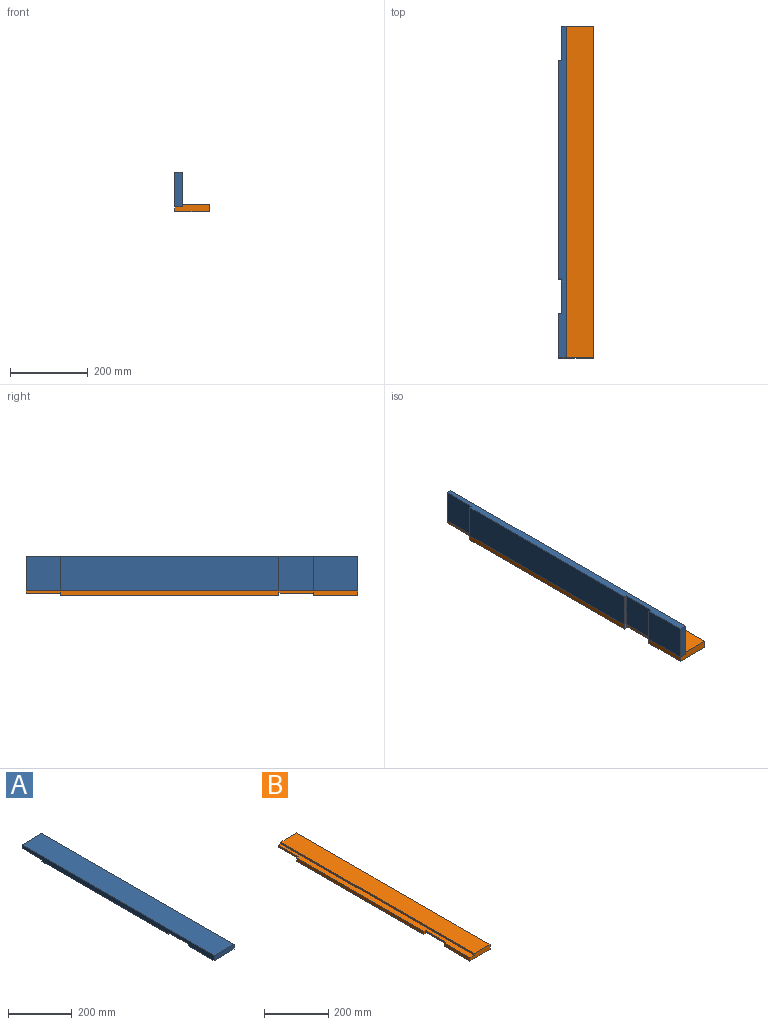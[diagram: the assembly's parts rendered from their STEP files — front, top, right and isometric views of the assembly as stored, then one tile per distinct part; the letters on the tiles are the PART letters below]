
ASSEMBLY  parts=2 mates=1
PART A: 12 faces, bbox 88.9x854.1x19.1 mm
  f0: plane 88.9x12.7mm, normal (0,1,0), area 1129mm2, adj f3,f4,f6,f11
  f1: plane 561.98x88.9mm, normal (0,0,-1), area 49959.6mm2, adj f3,f4,f7,f10
  f2: plane 114.3x88.9mm, normal (0,0,-1), area 10161.3mm2, adj f3,f4,f5,f8
  f3: plane 854.08x19.05mm, normal (-1,0,0), area 15141.1mm2, adj f0,f1,f2,f5,f6,f7,f8,f9
  f4: plane 854.08x19.05mm, normal (1,0,0), area 15141.1mm2, adj f0,f1,f2,f5,f6,f7,f8,f9
  f5: plane 88.9x19.05mm, normal (0,-1,0), area 1693.5mm2, adj f2,f3,f4,f6
  f6: plane 854.08x88.9mm, normal (0,0,1), area 75927.3mm2, adj f0,f3,f4,f5
  f7: plane 88.9x6.35mm, normal (0,-1,0), area 564.5mm2, adj f1,f3,f4,f9
  f8: plane 88.9x6.35mm, normal (0,1,0), area 564.5mm2, adj f2,f3,f4,f9
  f9: plane 88.9x88.9mm, normal (0,0,-1), area 7903.2mm2, adj f3,f4,f7,f8
  f10: plane 88.9x6.35mm, normal (0,1,0), area 564.5mm2, adj f1,f3,f4,f11
  f11: plane 88.9x88.9mm, normal (0,0,-1), area 7903.2mm2, adj f0,f3,f4,f10
PART B: 17 faces, bbox 88.9x854.1x19.1 mm
  f0: plane 82.55x12.7mm, normal (0,1,0), area 967.7mm2, adj f3,f4,f5,f7,f14,f16
  f1: plane 561.98x12.7mm, normal (-1,0,0), area 7137.1mm2, adj f4,f10,f11,f13
  f2: plane 88.9x82.55mm, normal (0,0,-1), area 7338.7mm2, adj f7,f11,f12,f15
  f3: plane 88.9x82.55mm, normal (0,0,-1), area 7338.7mm2, adj f0,f7,f13,f16
  f4: plane 854.08x19.05mm, normal (0,0,1), area 15141.1mm2, adj f0,f1,f8,f9,f11,f12,f13,f14
  f5: plane 854.08x69.85mm, normal (0,0,1), area 59657.1mm2, adj f0,f7,f9,f14
  f6: plane 114.3x88.9mm, normal (0,0,-1), area 10161.3mm2, adj f7,f8,f9,f12
  f7: plane 854.08x19.05mm, normal (1,0,0), area 15141.1mm2, adj f0,f2,f3,f5,f6,f9,f10,f11
  f8: plane 114.3x12.7mm, normal (-1,0,0), area 1451.6mm2, adj f4,f6,f9,f12
  f9: plane 88.9x19.05mm, normal (0,-1,0), area 1572.6mm2, adj f4,f5,f6,f7,f8,f14
  f10: plane 561.98x88.9mm, normal (0,0,-1), area 49959.6mm2, adj f1,f7,f11,f13
  f11: plane 88.9x12.7mm, normal (0,-1,0), area 604.8mm2, adj f1,f2,f4,f7,f10,f15
  f12: plane 88.9x12.7mm, normal (0,1,0), area 604.8mm2, adj f2,f4,f6,f7,f8,f15
  f13: plane 88.9x12.7mm, normal (0,1,0), area 604.8mm2, adj f1,f3,f4,f7,f10,f16
  f14: plane 854.08x6.35mm, normal (-1,0,0), area 5423.4mm2, adj f0,f4,f5,f9
  f15: plane 88.9x6.35mm, normal (-1,0,0), area 564.5mm2, adj f2,f4,f11,f12
  f16: plane 88.9x6.35mm, normal (-1,0,0), area 564.5mm2, adj f0,f3,f4,f13
PLACE A rot(axis=(0,1,0),90deg) t=(-181.58,226.27,-35.72)mm
PLACE B t=(-111.73,226.27,-156.37)mm
MATE fastened A.f4 <-> B.f4  axis (0,0,-1) through (-181.58,226.27,-162.72)mm
